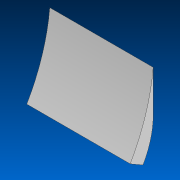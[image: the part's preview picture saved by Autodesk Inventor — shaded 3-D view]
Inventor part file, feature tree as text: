
AUTODESK INVENTOR PART (.ipt)
format: ipt  version: 2022 (Build 260153000, 153)  size: 120,320 bytes
history: native  units: in
note: dims shown in document units (in); Inventor stores cm internally (conversion verified against a paired STEP export)
features: sketch x2, extrude x1, hole x1, pattern_linear x1
ambient origin geometry x8: Origin, YZ Plane, XZ Plane, XY Plane, X Axis, Y Axis, Z Axis, Center Point
bodies: Solid1 (feature_tree)
feature tree (5):
  extrude  "Extrusion1"  Depth=1.0in
  hole  "Hole1"  [1 undecoded]
  pattern_linear  "Rectangular Pattern1"  Spacing1=1.5in  [1 undecoded]
  sketch  "Sketch1"  dims[d0=3.0in d1=1.0in]
  sketch  "Sketch2"  dims[d2=60.0deg d3=1.625in d4=1.5in d5=5.7814in d6=0.817in d7=9.0in d8=3.5in d9=7.0in d10=0.0in d11=0.5in d12=1.0in d13=0.175in d14=0.75in d15=0.22in d16=0.325in d17=0.5635in d18=1.5in d19=0.0in d20=2.3622in d22=1.0in]
note: 2 required parameter values undecoded (feature->parameter linkage not recoverable at this tier; creation-order binding heuristic only, values carry confidence <= 0.55)
